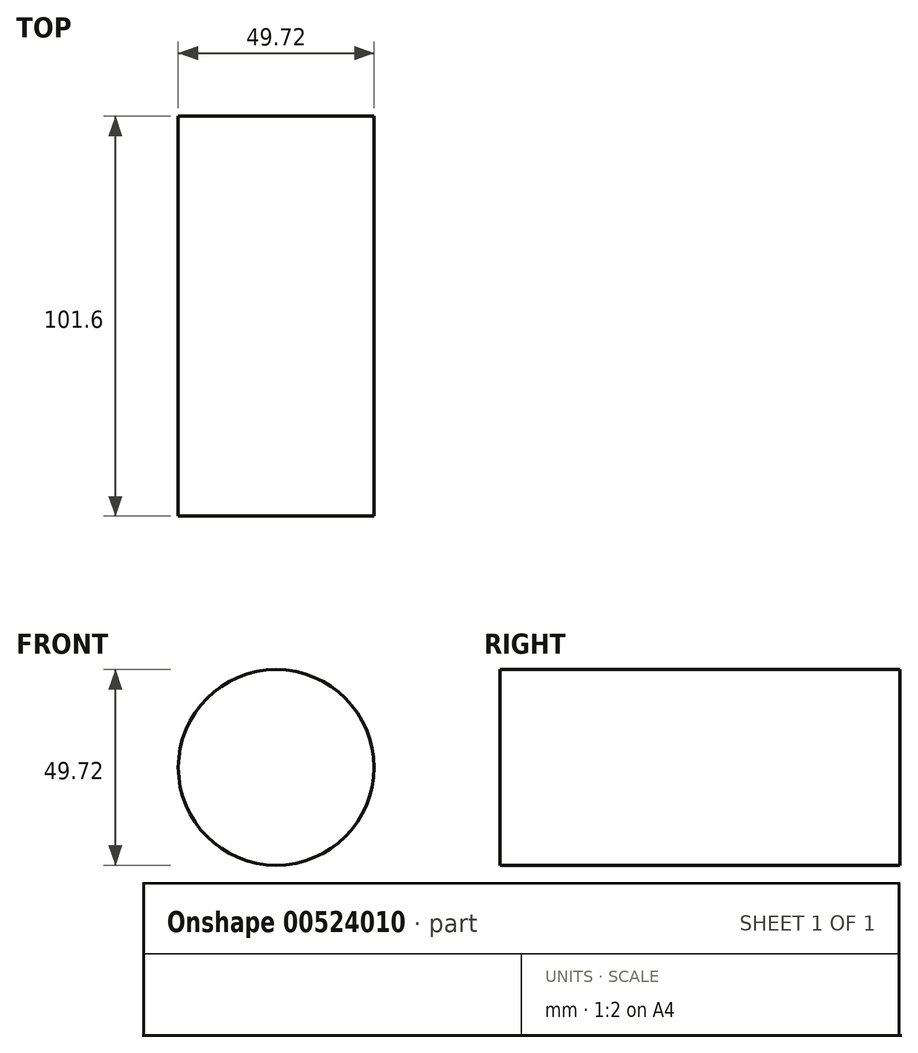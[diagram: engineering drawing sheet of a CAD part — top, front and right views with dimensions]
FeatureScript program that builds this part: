
annotation { "Feature Type Name" : "Feature", "Feature Type Description" : "" }
export const myFeature = defineFeature(function(context is Context, id is Id, definition is map)
    precondition{}
    {
        {
            var Q0;
            Q0=qCreatedBy(makeId("Front.planeOp"),FACE);
            var sketch = newSketch(context, id + "F0", { "sketchPlane" : qUnion([Q0])});
            skCircle(sketch, "E0", {"center": v(0, 0) * mm, "radius": 24.86 * mm});
            skSolve(sketch);
        }
        {
            var Q0;
            Q0 = qSketchRegion(id + "F0", true);
            extrude(context, id + "F1", {"entities" : qUnion([Q0]), "depth" : 101.6 * mm, "offsetDistance" : 25.4 * mm});
        }
    });
